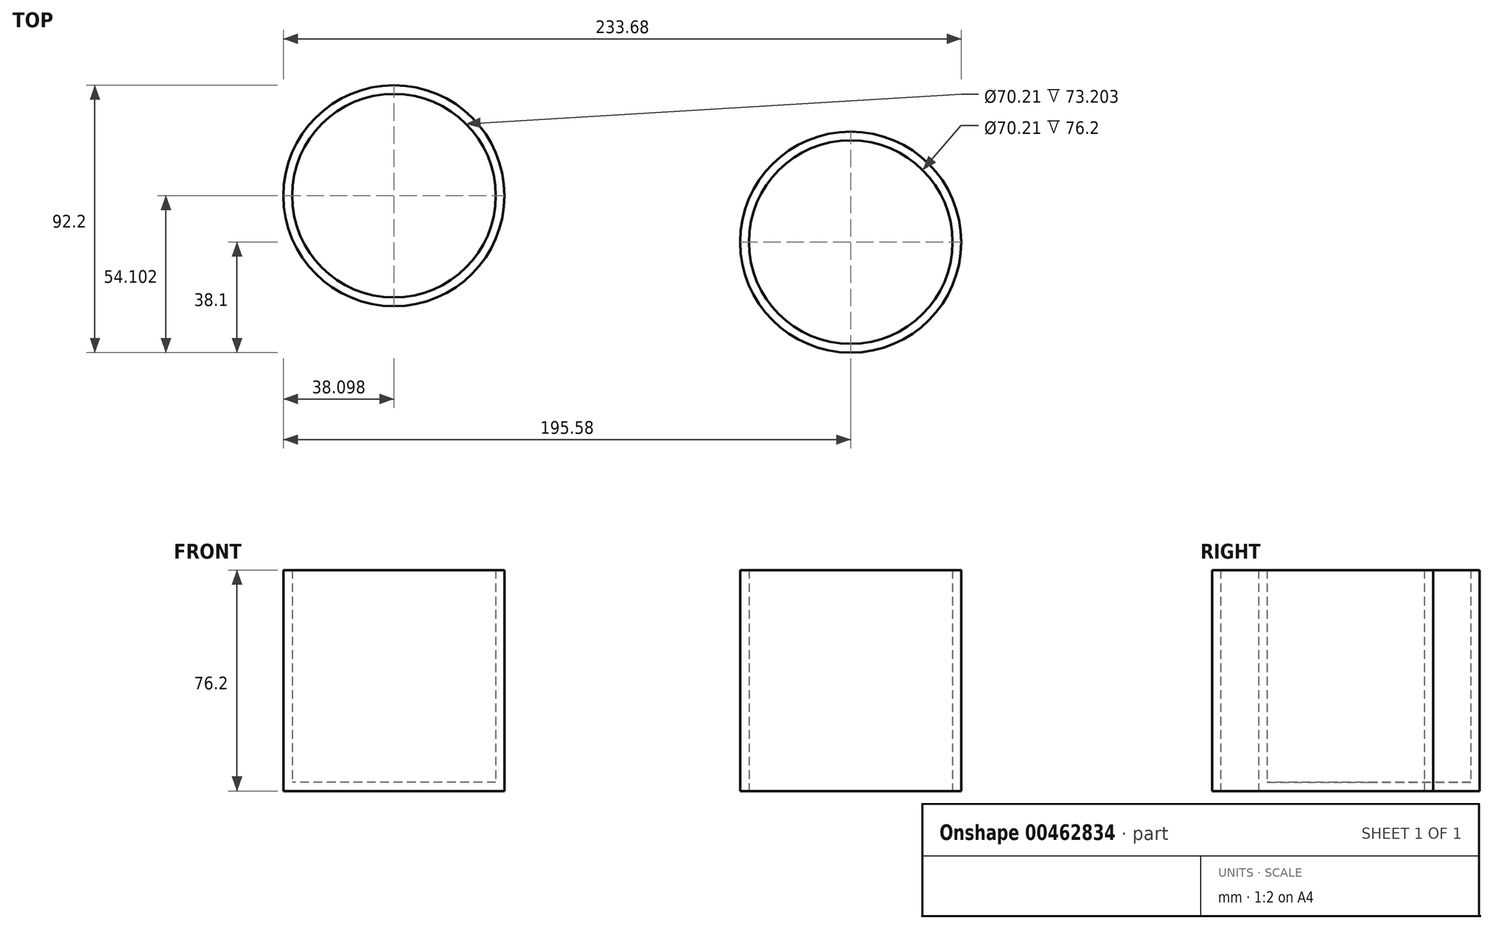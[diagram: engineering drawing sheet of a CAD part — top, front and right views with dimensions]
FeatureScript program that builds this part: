
annotation { "Feature Type Name" : "Feature", "Feature Type Description" : "" }
export const myFeature = defineFeature(function(context is Context, id is Id, definition is map)
    precondition{}
    {
        {
            var Q0;
            Q0=qCreatedBy(makeId("Top.planeOp"),FACE);
            var sketch = newSketch(context, id + "F0", { "sketchPlane" : qUnion([Q0])});
            skCircle(sketch, "E0", {"center": v(0, 0) * mm, "radius": 38.1 * mm});
            skSolve(sketch);
        }
        {
            var Q0;
            Q0=makeQuery(id+"F0.imprint","IMPRINT",FACE,{"disambiguationData":[TD([[makeQuery(id+"F0.imprint","IMPRINT",EDGE,{"derivedFrom":sQuery(id+"F0.wireOp",EDGE,"E0")}),1.0]])]});
            extrude(context, id + "F1", {"entities" : qUnion([Q0]), "depth" : 76.2 * mm});
        }
        {
            var Q0;
            Q0=qCreatedBy(makeId("Top.planeOp"),FACE);
            var sketch = newSketch(context, id + "F2", { "sketchPlane" : qUnion([Q0])});
            skCircle(sketch, "E1", {"center": v(-157.48, 16) * mm, "radius": 38.1 * mm});
            skSolve(sketch);
        }
        {
            var Q0;
            Q0=makeQuery(id+"F2.imprint","IMPRINT",FACE,{"disambiguationData":[TD([[makeQuery(id+"F2.imprint","IMPRINT",EDGE,{"derivedFrom":sQuery(id+"F2.wireOp",EDGE,"E1")}),1.0]])]});
            extrude(context, id + "F3", {"entities" : qUnion([Q0]), "depth" : 76.2 * mm});
        }
        {
            var Q0;
            Q0=makeQuery(id+"F3.opExtrude","CAP_FACE",FACE,{"disambiguationData":[OSD([sQuery(id+"F2.wireOp",EDGE,"E1")])],"isStart":false});
            shell(context, id + "F4", {"entities" : qUnion([Q0]), "thickness" : 3 * mm});
        }
        {
            var Q0;
            Q0=makeQuery(id+"F1.opExtrude","CAP_FACE",FACE,{"disambiguationData":[OSD([sQuery(id+"F0.wireOp",EDGE,"E0")])],"isStart":false});
            shell(context, id + "F5", {"entities" : qUnion([Q0]), "thickness" : 3 * mm});
        }
        {
            var Q0;
            {var subQ0=sQuery(id+"F0.wireOp",EDGE,"E0");Q0=makeQuery(id+"F5.opShell","OFFSET_FACE",FACE,{"disambiguationData":[OSD([subQ0]),TDD([makeQuery(id+"F1.opExtrude","CAP_FACE",FACE,{"disambiguationData":[OSD([subQ0])],"isStart":true})])]});}
            var sketch = newSketch(context, id + "F6", { "sketchPlane" : qUnion([Q0])});
            skCircle(sketch, "E2", {"center": v(0, 0) * mm, "radius": 35.28 * mm});
            skSolve(sketch);
        }
        {
            var Q0;
            {var subQ0=sQuery(id+"F0.wireOp",EDGE,"E0");Q0=makeQuery(id+"F6.imprint","IMPRINT",FACE,{"disambiguationData":[TD([[makeQuery(id+"F6.imprint","IMPRINT",EDGE,{"derivedFrom":makeQuery(id+"F5.opShell","OFFSET_EDGE",EDGE,{"disambiguationData":[OSD([subQ0]),TDD([makeQuery(id+"F1.opExtrude","CAP_EDGE",EDGE,{"disambiguationData":[OSD([subQ0])],"isStart":true})])]})}),1.0]])]});}
            extrude(context, id + "F7", {"entities" : qUnion([Q0]), "operationType" : NewBodyOperationType.REMOVE, "oppositeDirection" : true, "depth" : 25.4 * mm});
        }
    });
